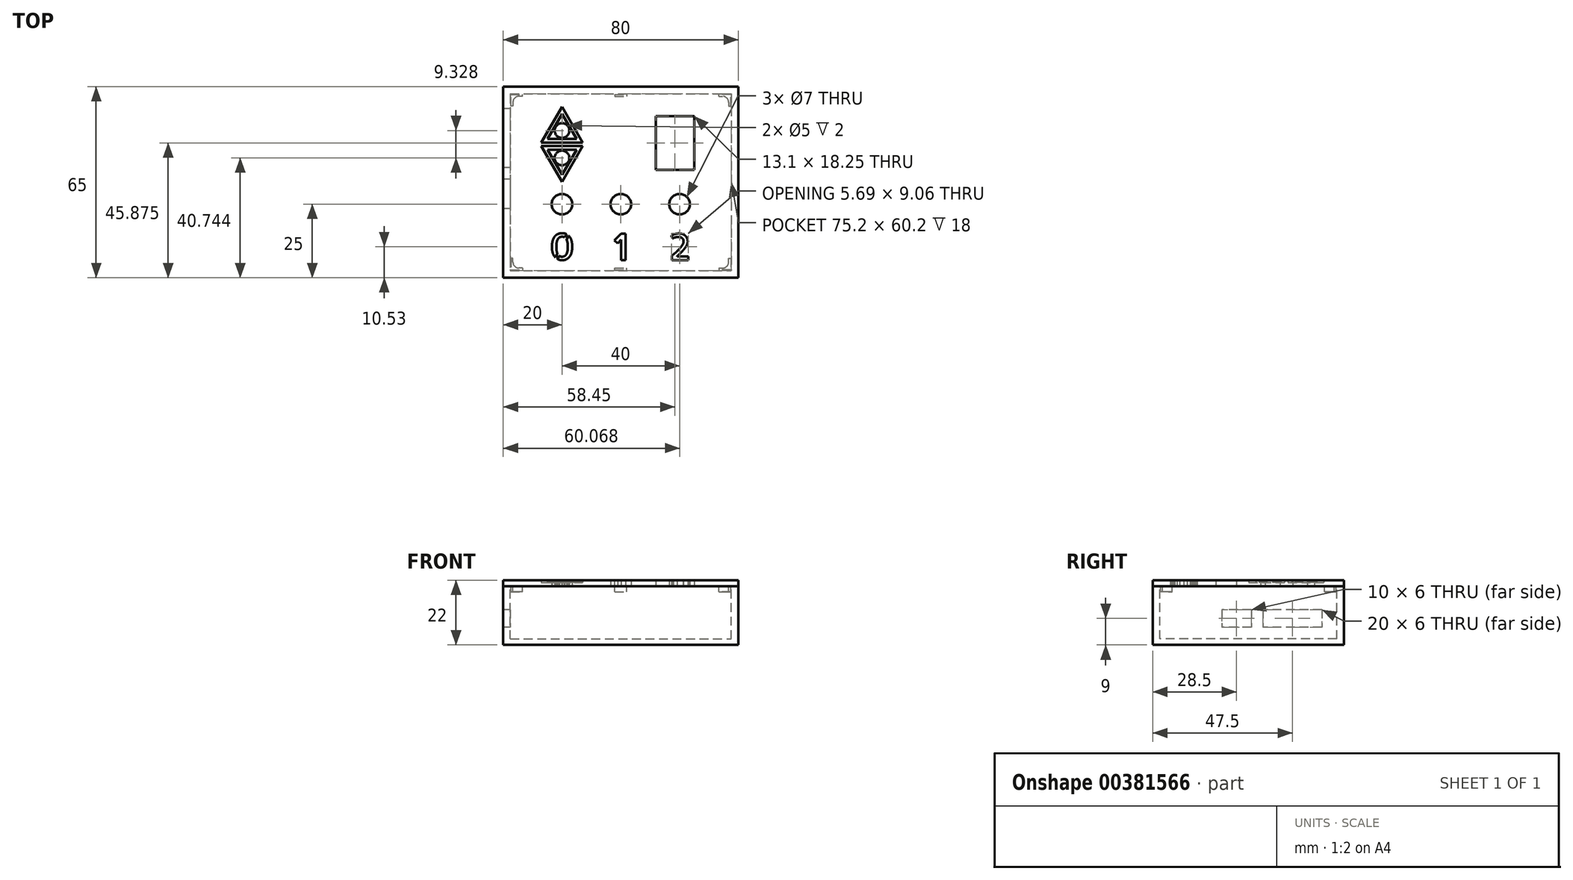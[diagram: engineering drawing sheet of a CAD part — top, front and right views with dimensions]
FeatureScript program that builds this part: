
annotation { "Feature Type Name" : "Feature", "Feature Type Description" : "" }
export const myFeature = defineFeature(function(context is Context, id is Id, definition is map)
    precondition{}
    {
        {
            var Q0;
            Q0=qCreatedBy(makeId("Top.planeOp"),FACE);
            var sketch = newSketch(context, id + "F0", { "sketchPlane" : qUnion([Q0])});
            skPoint(sketch, "E0.middle", {"position": v(0, 0) * mm});
            skLineSegment(sketch, "E1.bottom", {"start": v(45, 11.75) * mm, "end": v(31.9, 11.75) * mm});
            skLineSegment(sketch, "E1.top", {"start": v(45, 30) * mm, "end": v(31.9, 30) * mm});
            skLineSegment(sketch, "E1.left", {"start": v(45, 11.75) * mm, "end": v(45, 30) * mm});
            skLineSegment(sketch, "E1.right", {"start": v(31.9, 11.75) * mm, "end": v(31.9, 30) * mm});
            skPoint(sketch, "E1.middle", {"position": v(38.45, 20.88) * mm});
            skCircle(sketch, "E2", {"center": v(0, 0) * mm, "radius": 3.5 * mm});
            skPoint(sketch, "E3.1.0.0", {"position": v(20, 0) * mm});
            skCircle(sketch, "E3.1.0.1", {"center": v(20, 0) * mm, "radius": 3.5 * mm});
            skPoint(sketch, "E3.2.0.0", {"position": v(40, 0) * mm});
            skCircle(sketch, "E3.2.0.1", {"center": v(40, 0) * mm, "radius": 3.5 * mm});
            skLineSegment(sketch, "E3.direction1", {"start": v(0, 0) * mm, "end": v(20, 0) * mm, "construction": true});
            skLineSegment(sketch, "E4.bottom", {"start": v(60, 40) * mm, "end": v(-20, 40) * mm});
            skLineSegment(sketch, "E4.top", {"start": v(60, -25) * mm, "end": v(-20, -25) * mm});
            skLineSegment(sketch, "E4.left", {"start": v(60, 40) * mm, "end": v(60, -25) * mm});
            skLineSegment(sketch, "E4.right", {"start": v(-20, 40) * mm, "end": v(-20, -25) * mm});
            skLineSegment(sketch, "E5", {"start": v(0, 32) * mm, "end": v(-6, 21.6) * mm});
            skLineSegment(sketch, "E6", {"start": v(-6, 21.6) * mm, "end": v(6, 21.6) * mm});
            skLineSegment(sketch, "E7", {"start": v(6, 21.6) * mm, "end": v(0, 32) * mm});
            skLineSegment(sketch, "E8", {"start": v(0, 8.82) * mm, "end": v(6, 19.2) * mm});
            skLineSegment(sketch, "E9", {"start": v(6, 19.2) * mm, "end": v(-6, 19.2) * mm});
            skLineSegment(sketch, "E10", {"start": v(-6, 19.2) * mm, "end": v(0, 8.82) * mm});
            skPoint(sketch, "E11", {"position": v(0, 21.6) * mm});
            skPoint(sketch, "E12", {"position": v(0, 25.07) * mm});
            skCircle(sketch, "E13", {"center": v(0, 25.07) * mm, "radius": 2.5 * mm});
            skCircle(sketch, "E14", {"center": v(0, 15.74) * mm, "radius": 2.5 * mm});
            skLineSegment(sketch, "E15", {"start": v(-17.4, 37.4) * mm, "end": v(-13.4, 37.4) * mm});
            skLineSegment(sketch, "E16", {"start": v(-13.4, 36.7) * mm, "end": v(-14.7, 36.7) * mm});
            skLineSegment(sketch, "E17", {"start": v(-16.7, 34.7) * mm, "end": v(-16.7, 33.4) * mm});
            skLineSegment(sketch, "E18", {"start": v(-16.7, 33.4) * mm, "end": v(-17.4, 33.4) * mm});
            skLineSegment(sketch, "E19", {"start": v(-17.4, 33.4) * mm, "end": v(-17.4, 37.4) * mm});
            skLineSegment(sketch, "E20", {"start": v(-13.4, 36.7) * mm, "end": v(-13.4, 37.4) * mm});
            skLineSegment(sketch, "E21", {"start": v(20, 40) * mm, "end": v(20, -25) * mm, "construction": true});
            skLineSegment(sketch, "E22", {"start": v(-20, 7.5) * mm, "end": v(60, 7.5) * mm, "construction": true});
            skLineSegment(sketch, "E23.0", {"start": v(0, 30.8) * mm, "end": v(-4.96, 22.2) * mm});
            skLineSegment(sketch, "E23.1", {"start": v(4.96, 22.2) * mm, "end": v(0, 30.8) * mm});
            skLineSegment(sketch, "E23.2", {"start": v(-4.96, 22.2) * mm, "end": v(4.96, 22.2) * mm});
            skLineSegment(sketch, "E24.0", {"start": v(-4.96, 18.6) * mm, "end": v(0, 10.02) * mm});
            skLineSegment(sketch, "E24.1", {"start": v(4.96, 18.6) * mm, "end": v(-4.96, 18.6) * mm});
            skLineSegment(sketch, "E24.2", {"start": v(0, 10.02) * mm, "end": v(4.96, 18.6) * mm});
            skArc(sketch, "E25", {"start": v(-14.7, 36.7) * mm, "mid": v(-16.11, 36.11) * mm, "end": v(-16.7, 34.7) * mm});
            skLineSegment(sketch, "E26.MirrorCS", {"start": v(-16.7, -18.4) * mm, "end": v(-17.4, -18.4) * mm});
            skLineSegment(sketch, "E27.MirrorCS", {"start": v(-13.4, -21.7) * mm, "end": v(-13.4, -22.4) * mm});
            skLineSegment(sketch, "E28.MirrorCS", {"start": v(-13.4, -21.7) * mm, "end": v(-14.7, -21.7) * mm});
            skLineSegment(sketch, "E29.MirrorCS", {"start": v(-17.4, -18.4) * mm, "end": v(-17.4, -22.4) * mm});
            skArc(sketch, "E30.MirrorCS", {"start": v(-14.7, -21.7) * mm, "mid": v(-16.11, -21.11) * mm, "end": v(-16.7, -19.7) * mm});
            skLineSegment(sketch, "E31.MirrorCS", {"start": v(-17.4, -22.4) * mm, "end": v(-13.4, -22.4) * mm});
            skLineSegment(sketch, "E32.MirrorCS", {"start": v(-16.7, -19.7) * mm, "end": v(-16.7, -18.4) * mm});
            skLineSegment(sketch, "E33.MirrorCS", {"start": v(20, -25) * mm, "end": v(20, 40) * mm, "construction": true});
            skLineSegment(sketch, "E34.MirrorCS", {"start": v(56.7, -18.4) * mm, "end": v(57.4, -18.4) * mm});
            skLineSegment(sketch, "E35.MirrorCS", {"start": v(53.4, -21.7) * mm, "end": v(54.7, -21.7) * mm});
            skLineSegment(sketch, "E36.MirrorCS", {"start": v(57.4, -22.4) * mm, "end": v(53.4, -22.4) * mm});
            skLineSegment(sketch, "E37.MirrorCS", {"start": v(56.7, -19.7) * mm, "end": v(56.7, -18.4) * mm});
            skArc(sketch, "E38.MirrorCS", {"start": v(54.7, -21.7) * mm, "mid": v(56.11, -21.11) * mm, "end": v(56.7, -19.7) * mm});
            skLineSegment(sketch, "E39.MirrorCS", {"start": v(57.4, -18.4) * mm, "end": v(57.4, -22.4) * mm});
            skLineSegment(sketch, "E40.MirrorCS", {"start": v(53.4, -21.7) * mm, "end": v(53.4, -22.4) * mm});
            skLineSegment(sketch, "E41.MirrorCS", {"start": v(56.7, 33.4) * mm, "end": v(57.4, 33.4) * mm});
            skLineSegment(sketch, "E42.MirrorCS", {"start": v(53.4, 36.7) * mm, "end": v(53.4, 37.4) * mm});
            skLineSegment(sketch, "E43.MirrorCS", {"start": v(56.7, 34.7) * mm, "end": v(56.7, 33.4) * mm});
            skLineSegment(sketch, "E44.MirrorCS", {"start": v(57.4, 33.4) * mm, "end": v(57.4, 37.4) * mm});
            skLineSegment(sketch, "E45.MirrorCS", {"start": v(57.4, 37.4) * mm, "end": v(53.4, 37.4) * mm});
            skLineSegment(sketch, "E46.MirrorCS", {"start": v(53.4, 36.7) * mm, "end": v(54.7, 36.7) * mm});
            skArc(sketch, "E47.MirrorCS", {"start": v(54.7, 36.7) * mm, "mid": v(56.11, 36.11) * mm, "end": v(56.7, 34.7) * mm});
            skLineSegment(sketch, "E48.bottom", {"start": v(18, 37.4) * mm, "end": v(22, 37.4) * mm});
            skLineSegment(sketch, "E48.top", {"start": v(18, 36.7) * mm, "end": v(22, 36.7) * mm});
            skLineSegment(sketch, "E48.left", {"start": v(18, 37.4) * mm, "end": v(18, 36.7) * mm});
            skLineSegment(sketch, "E48.right", {"start": v(22, 37.4) * mm, "end": v(22, 36.7) * mm});
            skPoint(sketch, "E48.middle", {"position": v(20, 37.05) * mm});
            skLineSegment(sketch, "E49.MirrorCS", {"start": v(18, -22.4) * mm, "end": v(22, -22.4) * mm});
            skLineSegment(sketch, "E50.MirrorCS", {"start": v(22, -22.4) * mm, "end": v(22, -21.7) * mm});
            skLineSegment(sketch, "E51.MirrorCS", {"start": v(18, -21.7) * mm, "end": v(22, -21.7) * mm});
            skLineSegment(sketch, "E52.MirrorCS", {"start": v(18, -22.4) * mm, "end": v(18, -21.7) * mm});
            skPoint(sketch, "E53.MirrorP", {"position": v(20, -22.05) * mm});
            skLineSegment(sketch, "E54", {"start": v(-6, 21.6) * mm, "end": v(3.67, 27.2) * mm, "construction": true});
            skLineSegment(sketch, "E55", {"start": v(6, 21.6) * mm, "end": v(-2.87, 26.73) * mm, "construction": true});
            skLineSegment(sketch, "E56", {"start": v(6, 19.2) * mm, "end": v(-4.56, 13.1) * mm, "construction": true});
            skLineSegment(sketch, "E57", {"start": v(-6, 19.2) * mm, "end": v(3.85, 13.52) * mm, "construction": true});
            skText(sketch, "E58", { "text": "0", "fontName": "AllertaStencil-Regular.ttf"});
            skText(sketch, "E59", { "text": "1", "fontName": "AllertaStencil-Regular.ttf"});
            skText(sketch, "E60", { "text": "2", "fontName": "AllertaStencil-Regular.ttf"});
            skLineSegment(sketch, "E61.0", {"start": v(7.04, 21) * mm, "end": v(0, 33.2) * mm});
            skLineSegment(sketch, "E61.1", {"start": v(-7.04, 21) * mm, "end": v(7.04, 21) * mm});
            skLineSegment(sketch, "E61.2", {"start": v(0, 33.2) * mm, "end": v(-7.04, 21) * mm});
            skLineSegment(sketch, "E62.0", {"start": v(7.04, 19.8) * mm, "end": v(-7.04, 19.8) * mm});
            skLineSegment(sketch, "E62.1", {"start": v(0, 7.62) * mm, "end": v(7.04, 19.8) * mm});
            skLineSegment(sketch, "E62.2", {"start": v(-7.04, 19.8) * mm, "end": v(0, 7.62) * mm});
            const initialGuessF0  = {"E58": [-0.00432, -0.019, 1, 0, 0.009], "E59": [0.01752, -0.019, 1, 0, 0.009], "E60": [0.03626, -0.019, 1, 0, 0.009]};
            skSetInitialGuess(sketch, initialGuessF0);
            skSolve(sketch);
        }
        {
            var Q0;
            Q0=makeQuery(id+"F0.imprint","IMPRINT",FACE,{"disambiguationData":[TD([[makeQuery(id+"F0.imprint","IMPRINT",EDGE,{"derivedFrom":sQuery(id+"F0.wireOp",EDGE,"E1.bottom")}),1.0]])]});
            extrude(context, id + "F1", {"entities" : qUnion([Q0]), "depth" : 2 * mm});
        }
        {
            var Q0;
            Q0=makeQuery(id+"F0.imprint","IMPRINT",FACE,{"disambiguationData":[TD([[makeQuery(id+"F0.imprint","IMPRINT",EDGE,{"derivedFrom":sQuery(id+"F0.wireOp",EDGE,"E5")}),1.0]])]});
            var Q1;
            Q1=makeQuery(id+"F0.imprint","IMPRINT",FACE,{"disambiguationData":[TD([[makeQuery(id+"F0.imprint","IMPRINT",EDGE,{"derivedFrom":sQuery(id+"F0.wireOp",EDGE,"E8")}),1.0]])]});
            var Q2;
            Q2=makeQuery(id+"F0.imprint","IMPRINT",FACE,{"disambiguationData":[TD([[makeQuery(id+"F0.imprint","IMPRINT",EDGE,{"derivedFrom":sQuery(id+"F0.wireOp",EDGE,"E5")}),-1.0]])]});
            var Q3;
            Q3=makeQuery(id+"F0.imprint","IMPRINT",FACE,{"disambiguationData":[TD([[makeQuery(id+"F0.imprint","IMPRINT",EDGE,{"derivedFrom":sQuery(id+"F0.wireOp",EDGE,"E8")}),-1.0]])]});
            extrude(context, id + "F2", {"entities" : qUnion([Q0, Q1, Q2, Q3]), "operationType" : NewBodyOperationType.ADD, "depth" : 1.2 * mm});
        }
        {
            var Q0;
            Q0=makeQuery(id+"F0.imprint","IMPRINT",FACE,{"disambiguationData":[TD([[makeQuery(id+"F0.imprint","IMPRINT",EDGE,{"derivedFrom":sQuery(id+"F0.wireOp",EDGE,"E15")}),-1.0]])]});
            var Q1;
            Q1=makeQuery(id+"F0.imprint","IMPRINT",FACE,{"disambiguationData":[TD([[makeQuery(id+"F0.imprint","IMPRINT",EDGE,{"derivedFrom":sQuery(id+"F0.wireOp",EDGE,"91e45d3a-258b-433f-9793-da6addab62280.MirrorCS")}),1.0]])]});
            var Q2;
            Q2=makeQuery(id+"F0.imprint","IMPRINT",FACE,{"disambiguationData":[TD([[makeQuery(id+"F0.imprint","IMPRINT",EDGE,{"derivedFrom":sQuery(id+"F0.wireOp",EDGE,"11152814-b426-4005-ae1a-6a1455c401de8.MirrorCS")}),1.0]])]});
            var Q3;
            Q3=makeQuery(id+"F0.imprint","IMPRINT",FACE,{"disambiguationData":[TD([[makeQuery(id+"F0.imprint","IMPRINT",EDGE,{"derivedFrom":sQuery(id+"F0.wireOp",EDGE,"11152814-b426-4005-ae1a-6a1455c401de0.MirrorCS")}),1.0]])]});
            var Q4;
            Q4=makeQuery(id+"F0.imprint","IMPRINT",FACE,{"disambiguationData":[TD([[makeQuery(id+"F0.imprint","IMPRINT",EDGE,{"derivedFrom":sQuery(id+"F0.wireOp",EDGE,"E41.MirrorCS")}),1.0]])]});
            var Q5;
            Q5=makeQuery(id+"F0.imprint","IMPRINT",FACE,{"disambiguationData":[TD([[makeQuery(id+"F0.imprint","IMPRINT",EDGE,{"derivedFrom":sQuery(id+"F0.wireOp",EDGE,"E34.MirrorCS")}),-1.0]])]});
            var Q6;
            Q6=makeQuery(id+"F0.imprint","IMPRINT",FACE,{"disambiguationData":[TD([[makeQuery(id+"F0.imprint","IMPRINT",EDGE,{"derivedFrom":sQuery(id+"F0.wireOp",EDGE,"E26.MirrorCS")}),1.0]])]});
            var Q7;
            Q7=makeQuery(id+"F0.imprint","IMPRINT",FACE,{"disambiguationData":[TD([[makeQuery(id+"F0.imprint","IMPRINT",EDGE,{"derivedFrom":sQuery(id+"F0.wireOp",EDGE,"E49.MirrorCS")}),1.0]])]});
            var Q8;
            Q8=makeQuery(id+"F0.imprint","IMPRINT",FACE,{"disambiguationData":[TD([[makeQuery(id+"F0.imprint","IMPRINT",EDGE,{"derivedFrom":sQuery(id+"F0.wireOp",EDGE,"E48.bottom")}),-1.0]])]});
            extrude(context, id + "F3", {"entities" : qUnion([Q0, Q1, Q2, Q3, Q4, Q5, Q6, Q7, Q8]), "operationType" : NewBodyOperationType.ADD, "oppositeDirection" : true, "depth" : 2 * mm, "hasSecondDirection" : true, "secondDirectionOppositeDirection" : false, "secondDirectionDepth" : 2 * mm});
        }
        {
            var Q0;
            Q0=makeQuery(id+"F0.imprint","IMPRINT",FACE,{"disambiguationData":[TD([[makeQuery(id+"F0.imprint","IMPRINT",EDGE,{"derivedFrom":sQuery(id+"F0.wireOp",EDGE,"E13")}),-1.0]])]});
            var Q1;
            Q1=makeQuery(id+"F0.imprint","IMPRINT",FACE,{"disambiguationData":[TD([[makeQuery(id+"F0.imprint","IMPRINT",EDGE,{"derivedFrom":sQuery(id+"F0.wireOp",EDGE,"E14")}),-1.0]])]});
            extrude(context, id + "F4", {"entities" : qUnion([Q0, Q1]), "operationType" : NewBodyOperationType.ADD, "depth" : 2 * mm});
        }
        {
            var Q0;
            Q0=qCreatedBy(makeId("Top.planeOp"),FACE);
            var sketch = newSketch(context, id + "F5", { "sketchPlane" : qUnion([Q0])});
            skLineSegment(sketch, "E63.bottom", {"start": v(-20, 40) * mm, "end": v(60, 40) * mm});
            skLineSegment(sketch, "E63.top", {"start": v(-20, -25) * mm, "end": v(60, -25) * mm});
            skLineSegment(sketch, "E63.left", {"start": v(-20, 40) * mm, "end": v(-20, -25) * mm});
            skLineSegment(sketch, "E63.right", {"start": v(60, 40) * mm, "end": v(60, -25) * mm});
            skLineSegment(sketch, "E64.0", {"start": v(-17.6, 37.6) * mm, "end": v(57.6, 37.6) * mm});
            skLineSegment(sketch, "E64.1", {"start": v(-17.6, 37.6) * mm, "end": v(-17.6, -22.6) * mm});
            skLineSegment(sketch, "E64.2", {"start": v(-17.6, -22.6) * mm, "end": v(57.6, -22.6) * mm});
            skLineSegment(sketch, "E64.3", {"start": v(57.6, 37.6) * mm, "end": v(57.6, -22.6) * mm});
            skSolve(sketch);
        }
        {
            var Q0;
            Q0=makeQuery(id+"F5.imprint","IMPRINT",FACE,{"disambiguationData":[TD([[makeQuery(id+"F5.imprint","IMPRINT",EDGE,{"derivedFrom":sQuery(id+"F5.wireOp",EDGE,"E63.bottom")}),-1.0]])]});
            extrude(context, id + "F6", {"entities" : qUnion([Q0]), "oppositeDirection" : true, "depth" : 20 * mm});
        }
        {
            var Q0;
            Q0=makeQuery(id+"F5.imprint","IMPRINT",FACE,{"disambiguationData":[TD([[makeQuery(id+"F5.imprint","IMPRINT",EDGE,{"derivedFrom":sQuery(id+"F5.wireOp",EDGE,"E64.0")}),-1.0]])]});
            extrude(context, id + "F7", {"entities" : qUnion([Q0]), "operationType" : NewBodyOperationType.ADD, "oppositeDirection" : true, "depth" : 20 * mm, "hasSecondDirection" : true, "secondDirectionOppositeDirection" : true, "secondDirectionDepth" : 18 * mm});
        }
        {
            var Q0;
            Q0=makeQuery(id+"F6.opExtrude","SWEPT_FACE",FACE,{"disambiguationData":[OSD([sQuery(id+"F5.wireOp",EDGE,"E63.left")])]});
            cPlane(context, id + "F8", {"entities" : qUnion([Q0]), "cplaneType" : CPlaneType.OFFSET, "offset" : 0 * mm, "width" : 150 * mm, "height" : 150 * mm});
        }
        {
            var Q0;
            Q0=qCreatedBy(id+"F8.planeOp",FACE);
            var sketch = newSketch(context, id + "F9", { "sketchPlane" : qUnion([Q0])});
            skLineSegment(sketch, "E65.bottom", {"start": v(-32.5, -8) * mm, "end": v(-12.5, -8) * mm});
            skLineSegment(sketch, "E65.top", {"start": v(-32.5, -14) * mm, "end": v(-12.5, -14) * mm});
            skLineSegment(sketch, "E65.left", {"start": v(-32.5, -8) * mm, "end": v(-32.5, -14) * mm});
            skLineSegment(sketch, "E65.right", {"start": v(-12.5, -8) * mm, "end": v(-12.5, -14) * mm});
            skPoint(sketch, "E65.middle", {"position": v(-7.5, -10) * mm});
            skLineSegment(sketch, "E66", {"start": v(-40, -10) * mm, "end": v(25, -10) * mm, "construction": true});
            skLineSegment(sketch, "E67.bottom", {"start": v(-8.5, -8) * mm, "end": v(1.5, -8) * mm});
            skLineSegment(sketch, "E67.top", {"start": v(-8.5, -14) * mm, "end": v(1.5, -14) * mm});
            skLineSegment(sketch, "E67.left", {"start": v(-8.5, -8) * mm, "end": v(-8.5, -14) * mm});
            skLineSegment(sketch, "E67.right", {"start": v(1.5, -8) * mm, "end": v(1.5, -14) * mm});
            skSolve(sketch);
        }
        {
            var Q0;
            Q0=makeQuery(id+"F9.imprint","IMPRINT",FACE,{"disambiguationData":[TD([[makeQuery(id+"F9.imprint","IMPRINT",EDGE,{"derivedFrom":sQuery(id+"F9.wireOp",EDGE,"E65.bottom")}),-1.0]])]});
            var Q1;
            Q1=makeQuery(id+"F9.imprint","IMPRINT",FACE,{"disambiguationData":[TD([[makeQuery(id+"F9.imprint","IMPRINT",EDGE,{"derivedFrom":sQuery(id+"F9.wireOp",EDGE,"1eb58284-25ee-46f5-911a-d3de6e85f728.1.0.0")}),-1.0]])]});
            var Q2;
            Q2=makeQuery(id+"F9.imprint","IMPRINT",FACE,{"disambiguationData":[TD([[makeQuery(id+"F9.imprint","IMPRINT",EDGE,{"derivedFrom":sQuery(id+"F9.wireOp",EDGE,"E67.bottom")}),-1.0]])]});
            extrude(context, id + "F10", {"entities" : qUnion([Q0, Q1, Q2]), "operationType" : NewBodyOperationType.REMOVE, "oppositeDirection" : true, "depth" : 5 * mm});
        }
    });
